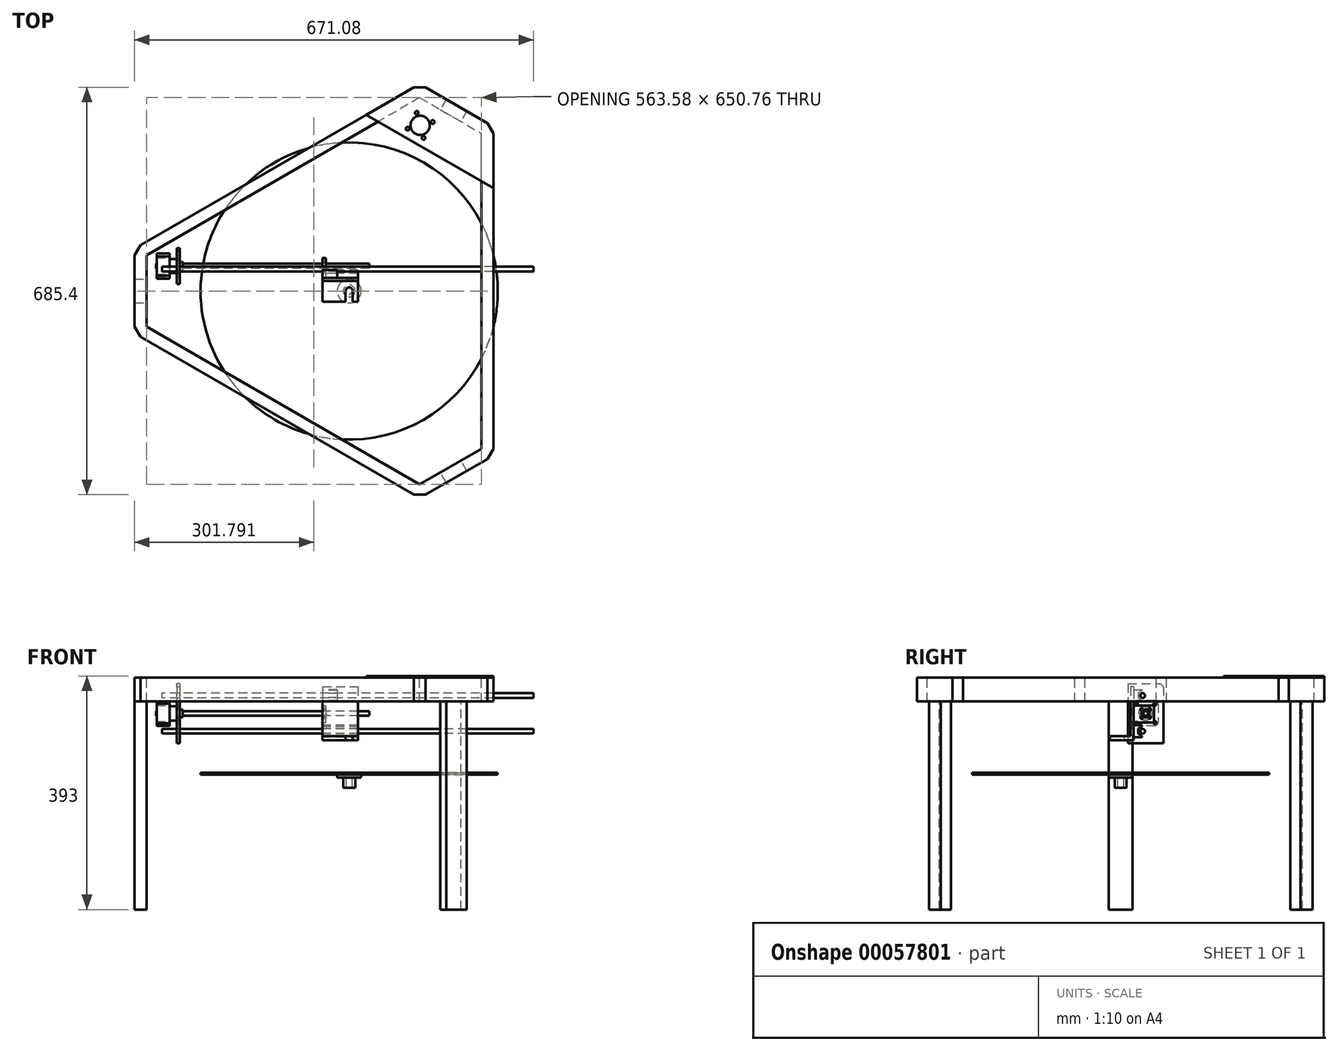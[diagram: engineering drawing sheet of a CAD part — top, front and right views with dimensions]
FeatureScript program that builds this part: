
annotation { "Feature Type Name" : "Feature", "Feature Type Description" : "" }
export const myFeature = defineFeature(function(context is Context, id is Id, definition is map)
    precondition{}
    {
        {
            var Q0;
            Q0=qCreatedBy(makeId("Right.planeOp"),FACE);
            var sketch = newSketch(context, id + "F0", { "sketchPlane" : qUnion([Q0])});
            skLineSegment(sketch, "E0.rect.bottom", {"start": v(21.15, 21.3) * mm, "end": v(-21.15, 21.3) * mm});
            skLineSegment(sketch, "E0.rect.top", {"start": v(21.15, -21.3) * mm, "end": v(-21.15, -21.3) * mm});
            skLineSegment(sketch, "E0.rect.left", {"start": v(21.15, 21.3) * mm, "end": v(21.15, -21.3) * mm});
            skLineSegment(sketch, "E0.rect.right", {"start": v(-21.15, 21.3) * mm, "end": v(-21.15, -21.3) * mm});
            skPoint(sketch, "E0.rect.middle", {"position": v(0, 0) * mm});
            skCircle(sketch, "E1", {"center": v(0, 0) * mm, "radius": 11 * mm});
            skCircle(sketch, "E2", {"center": v(0, 0) * mm, "radius": 4 * mm});
            skCircle(sketch, "E3", {"center": v(0, 0) * mm, "radius": 6.5 * mm});
            skCircle(sketch, "E4", {"center": v(0, 0) * mm, "radius": 12 * mm});
            skLineSegment(sketch, "E5", {"start": v(0, 0) * mm, "end": v(0, -54.1) * mm, "construction": true});
            skLineSegment(sketch, "E6", {"start": v(1.43, 0) * mm, "end": v(43.12, 0) * mm, "construction": true});
            skPoint(sketch, "E6.endSnap0", {"position": v(21.15, 0) * mm});
            skCircle(sketch, "E7", {"center": v(-15.5, -15.5) * mm, "radius": 2 * mm});
            skCircle(sketch, "E8.MirrorC", {"center": v(15.5, -15.5) * mm, "radius": 2 * mm});
            skCircle(sketch, "E9.MirrorC", {"center": v(-15.5, 15.5) * mm, "radius": 2 * mm});
            skCircle(sketch, "E10.MirrorC", {"center": v(15.5, 15.5) * mm, "radius": 2 * mm});
            skSolve(sketch);
        }
        {
            var Q0;
            Q0=makeQuery(id+"F0.imprint","IMPRINT",FACE,{"disambiguationData":[TD([[makeQuery(id+"F0.imprint","IMPRINT",EDGE,{"derivedFrom":sQuery(id+"F0.wireOp",EDGE,"E0.rect.bottom")}),1.0]])]});
            var Q1;
            Q1=makeQuery(id+"F0.imprint","IMPRINT",FACE,{"disambiguationData":[TD([[makeQuery(id+"F0.imprint","IMPRINT",EDGE,{"derivedFrom":sQuery(id+"F0.wireOp",EDGE,"E9.MirrorC")}),-1.0]])]});
            var Q2;
            Q2=makeQuery(id+"F0.imprint","IMPRINT",FACE,{"disambiguationData":[TD([[makeQuery(id+"F0.imprint","IMPRINT",EDGE,{"derivedFrom":sQuery(id+"F0.wireOp",EDGE,"E10.MirrorC")}),1.0]])]});
            var Q3;
            Q3=makeQuery(id+"F0.imprint","IMPRINT",FACE,{"disambiguationData":[TD([[makeQuery(id+"F0.imprint","IMPRINT",EDGE,{"derivedFrom":sQuery(id+"F0.wireOp",EDGE,"E8.MirrorC")}),-1.0]])]});
            var Q4;
            Q4=makeQuery(id+"F0.imprint","IMPRINT",FACE,{"disambiguationData":[TD([[makeQuery(id+"F0.imprint","IMPRINT",EDGE,{"derivedFrom":sQuery(id+"F0.wireOp",EDGE,"E7")}),1.0]])]});
            var Q5;
            Q5=makeQuery(id+"F0.imprint","IMPRINT",FACE,{"disambiguationData":[TD([[makeQuery(id+"F0.imprint","IMPRINT",EDGE,{"derivedFrom":sQuery(id+"F0.wireOp",EDGE,"E1")}),-1.0]])]});
            var Q6;
            Q6=makeQuery(id+"F0.imprint","IMPRINT",FACE,{"disambiguationData":[TD([[makeQuery(id+"F0.imprint","IMPRINT",EDGE,{"derivedFrom":sQuery(id+"F0.wireOp",EDGE,"E1")}),1.0]])]});
            var Q7;
            Q7=makeQuery(id+"F0.imprint","IMPRINT",FACE,{"disambiguationData":[TD([[makeQuery(id+"F0.imprint","IMPRINT",EDGE,{"derivedFrom":sQuery(id+"F0.wireOp",EDGE,"E2")}),-1.0]])]});
            extrude(context, id + "F1", {"entities" : qUnion([Q0, Q1, Q2, Q3, Q4, Q5, Q6, Q7]), "oppositeDirection" : true, "depth" : 34 * mm});
        }
        {
            var Q0;
            Q0=makeQuery(id+"F0.imprint","IMPRINT",FACE,{"disambiguationData":[TD([[makeQuery(id+"F0.imprint","IMPRINT",EDGE,{"derivedFrom":sQuery(id+"F0.wireOp",EDGE,"E2")}),1.0]])]});
            extrude(context, id + "F2", {"entities" : qUnion([Q0]), "depth" : 324 * mm, "hasSecondDirection" : true, "secondDirectionOppositeDirection" : true, "secondDirectionDepth" : 35 * mm});
        }
        {
            var Q0;
            Q0=makeQuery(id+"F0.imprint","IMPRINT",FACE,{"disambiguationData":[TD([[makeQuery(id+"F0.imprint","IMPRINT",EDGE,{"derivedFrom":sQuery(id+"F0.wireOp",EDGE,"E1")}),1.0]])]});
            var Q1;
            Q1=makeQuery(id+"F0.imprint","IMPRINT",FACE,{"disambiguationData":[TD([[makeQuery(id+"F0.imprint","IMPRINT",EDGE,{"derivedFrom":sQuery(id+"F0.wireOp",EDGE,"E2")}),-1.0]])]});
            extrude(context, id + "F3", {"entities" : qUnion([Q0, Q1]), "operationType" : NewBodyOperationType.ADD, "depth" : 2 * mm});
        }
        {
            var Q0;
            Q0=makeQuery(id+"F1.opExtrude","SWEPT_EDGE",EDGE,{"disambiguationData":[OSD([sQuery(id+"F0.wireOp",EDGE,"E0.rect.bottom"),sQuery(id+"F0.wireOp",EDGE,"E0.rect.left")])]});
            var Q1;
            Q1=makeQuery(id+"F1.opExtrude","SWEPT_EDGE",EDGE,{"disambiguationData":[OSD([sQuery(id+"F0.wireOp",EDGE,"E0.rect.top"),sQuery(id+"F0.wireOp",EDGE,"E0.rect.left")])]});
            var Q2;
            Q2=makeQuery(id+"F1.opExtrude","SWEPT_EDGE",EDGE,{"disambiguationData":[OSD([sQuery(id+"F0.wireOp",EDGE,"E0.rect.bottom"),sQuery(id+"F0.wireOp",EDGE,"E0.rect.right")])]});
            var Q3;
            Q3=makeQuery(id+"F1.opExtrude","SWEPT_EDGE",EDGE,{"disambiguationData":[OSD([sQuery(id+"F0.wireOp",EDGE,"E0.rect.top"),sQuery(id+"F0.wireOp",EDGE,"E0.rect.right")])]});
            chamfer(context, id + "F4", {"entities" : qUnion([Q0, Q1, Q2, Q3]), "width" : 5 * mm, "tangentPropagation" : true});
        }
        {
            var Q0;
            Q0=makeQuery(id+"F0.imprint","IMPRINT",FACE,{"disambiguationData":[TD([[makeQuery(id+"F0.imprint","IMPRINT",EDGE,{"derivedFrom":sQuery(id+"F0.wireOp",EDGE,"E10.MirrorC")}),1.0]])]});
            var Q1;
            Q1=makeQuery(id+"F0.imprint","IMPRINT",FACE,{"disambiguationData":[TD([[makeQuery(id+"F0.imprint","IMPRINT",EDGE,{"derivedFrom":sQuery(id+"F0.wireOp",EDGE,"E9.MirrorC")}),-1.0]])]});
            var Q2;
            Q2=makeQuery(id+"F0.imprint","IMPRINT",FACE,{"disambiguationData":[TD([[makeQuery(id+"F0.imprint","IMPRINT",EDGE,{"derivedFrom":sQuery(id+"F0.wireOp",EDGE,"E7")}),1.0]])]});
            var Q3;
            Q3=makeQuery(id+"F0.imprint","IMPRINT",FACE,{"disambiguationData":[TD([[makeQuery(id+"F0.imprint","IMPRINT",EDGE,{"derivedFrom":sQuery(id+"F0.wireOp",EDGE,"E8.MirrorC")}),-1.0]])]});
            extrude(context, id + "F5", {"entities" : qUnion([Q0, Q1, Q2, Q3]), "operationType" : NewBodyOperationType.REMOVE, "oppositeDirection" : true, "depth" : 12 * mm});
        }
        {
            var Q0;
            Q0=makeQuery(id+"F0.imprint","IMPRINT",FACE,{"disambiguationData":[TD([[makeQuery(id+"F0.imprint","IMPRINT",EDGE,{"derivedFrom":sQuery(id+"F0.wireOp",EDGE,"E2")}),-1.0]])]});
            extrude(context, id + "F6", {"entities" : qUnion([Q0]), "depth" : 10.2 * mm});
        }
        {
            var Q0;
            Q0=makeQuery(id+"F0.imprint","IMPRINT",FACE,{"disambiguationData":[TD([[makeQuery(id+"F0.imprint","IMPRINT",EDGE,{"derivedFrom":sQuery(id+"F0.wireOp",EDGE,"E1")}),1.0]])]});
            var Q1;
            Q1=makeQuery(id+"F0.imprint","IMPRINT",FACE,{"disambiguationData":[TD([[makeQuery(id+"F0.imprint","IMPRINT",EDGE,{"derivedFrom":sQuery(id+"F0.wireOp",EDGE,"E1")}),-1.0]])]});
            extrude(context, id + "F7", {"entities" : qUnion([Q0, Q1]), "operationType" : NewBodyOperationType.ADD, "depth" : 4.1 * mm});
        }
        {
            var Q0;
            Q0=qCreatedBy(makeId("Right.planeOp"),FACE);
            var sketch = newSketch(context, id + "F8", { "sketchPlane" : qUnion([Q0])});
            skCircle(sketch, "E11", {"center": v(0, 0) * mm, "radius": 9.5 * mm, "construction": true});
            skCircle(sketch, "E12", {"center": v(6.72, 6.72) * mm, "radius": 1.6 * mm});
            skLineSegment(sketch, "E13", {"start": v(0, 0) * mm, "end": v(21.23, 0) * mm, "construction": true});
            skLineSegment(sketch, "E14", {"start": v(0, 0) * mm, "end": v(0, 18.12) * mm, "construction": true});
            skLineSegment(sketch, "E15", {"start": v(0, 0) * mm, "end": v(6.72, 6.72) * mm, "construction": true});
            skCircle(sketch, "E16.MirrorC", {"center": v(6.72, -6.72) * mm, "radius": 1.6 * mm});
            skCircle(sketch, "E17.MirrorC", {"center": v(-6.72, 6.72) * mm, "radius": 1.6 * mm});
            skCircle(sketch, "E18.MirrorC", {"center": v(-6.72, -6.72) * mm, "radius": 1.6 * mm});
            skSolve(sketch);
        }
        {
            var Q0;
            Q0=qSketchRegion(id+"F8",true);
            extrude(context, id + "F9", {"entities" : qUnion([Q0]), "operationType" : NewBodyOperationType.REMOVE, "endBound" : BoundingType.THROUGH_ALL, "depth" : 25 * mm});
        }
        {
            var Q0;
            Q0=qCreatedBy(makeId("Top.planeOp"),FACE);
            var sketch = newSketch(context, id + "F10", { "sketchPlane" : qUnion([Q0])});
            skCircle(sketch, "E19", {"center": v(290, 0) * mm, "radius": 260 * mm, "construction": true});
            skLineSegment(sketch, "E20", {"start": v(0, 0) * mm, "end": v(0, 131.8) * mm, "construction": true});
            skLineSegment(sketch, "E21", {"start": v(290, 0) * mm, "end": v(290, -42) * mm, "construction": true});
            skCircle(sketch, "E22", {"center": v(290, -42) * mm, "radius": 250 * mm, "construction": true});
            skLineSegment(sketch, "E23.rect.bottom", {"start": v(305, -20) * mm, "end": v(245, -20) * mm});
            skLineSegment(sketch, "E23.rect.top", {"start": v(305, -60) * mm, "end": v(245, -60) * mm});
            skLineSegment(sketch, "E23.rect.left", {"start": v(305, -20) * mm, "end": v(305, -60) * mm});
            skLineSegment(sketch, "E23.rect.right", {"start": v(245, -20) * mm, "end": v(245, -60) * mm});
            skPoint(sketch, "E23.rect.middle", {"position": v(275, -40) * mm});
            skLineSegment(sketch, "E24", {"start": v(0, 0) * mm, "end": v(-84.34, 0) * mm, "construction": true});
            skLineSegment(sketch, "E25.bottom", {"start": v(245, -20) * mm, "end": v(269, -20) * mm});
            skLineSegment(sketch, "E25.top", {"start": v(245, 1.5) * mm, "end": v(269, 1.5) * mm});
            skLineSegment(sketch, "E25.left", {"start": v(245, -20) * mm, "end": v(245, 1.5) * mm});
            skLineSegment(sketch, "E25.right", {"start": v(269, -20) * mm, "end": v(269, 1.5) * mm});
            skLineSegment(sketch, "E26.bottom", {"start": v(305, -20) * mm, "end": v(281, -20) * mm});
            skLineSegment(sketch, "E26.top", {"start": v(305, 1.5) * mm, "end": v(281, 1.5) * mm});
            skLineSegment(sketch, "E26.left", {"start": v(305, -20) * mm, "end": v(305, 1.5) * mm});
            skLineSegment(sketch, "E26.right", {"start": v(281, -20) * mm, "end": v(281, 1.5) * mm});
            skLineSegment(sketch, "E27", {"start": v(245, -13.5) * mm, "end": v(269, -13.5) * mm});
            skLineSegment(sketch, "E28", {"start": v(281, -13.5) * mm, "end": v(290, -13.5) * mm});
            skPoint(sketch, "E28.startSnap0", {"position": v(257, -13.5) * mm});
            skLineSegment(sketch, "E29", {"start": v(257, -13.5) * mm, "end": v(257, 1.5) * mm});
            skPoint(sketch, "E30", {"position": v(257, -6) * mm});
            skLineSegment(sketch, "E31", {"start": v(491.95, -12) * mm, "end": v(676.1, -12) * mm, "construction": true});
            skLineSegment(sketch, "E32", {"start": v(257, -6) * mm, "end": v(462, -6) * mm, "construction": true});
            skLineSegment(sketch, "E33.rect.bottom", {"start": v(450, 1.5) * mm, "end": v(474, 1.5) * mm});
            skLineSegment(sketch, "E33.rect.top", {"start": v(450, -13.5) * mm, "end": v(474, -13.5) * mm});
            skLineSegment(sketch, "E33.rect.left", {"start": v(450, 1.5) * mm, "end": v(450, -13.5) * mm});
            skLineSegment(sketch, "E33.rect.right", {"start": v(474, 1.5) * mm, "end": v(474, -13.5) * mm});
            skPoint(sketch, "E33.rect.middle", {"position": v(462, -6) * mm});
            skLineSegment(sketch, "E34.rect.bottom", {"start": v(486, 1.5) * mm, "end": v(510, 1.5) * mm});
            skLineSegment(sketch, "E34.rect.top", {"start": v(486, -13.5) * mm, "end": v(510, -13.5) * mm});
            skLineSegment(sketch, "E34.rect.left", {"start": v(486, 1.5) * mm, "end": v(486, -13.5) * mm});
            skLineSegment(sketch, "E34.rect.right", {"start": v(510, 1.5) * mm, "end": v(510, -13.5) * mm});
            skPoint(sketch, "E34.rect.middle", {"position": v(498, -6) * mm});
            skPoint(sketch, "E34.rect.middle.positionSnap0", {"position": v(474, -6) * mm});
            skPoint(sketch, "E34.rect.centerSnap0", {"position": v(474, -6) * mm});
            skLineSegment(sketch, "E35.bottom", {"start": v(450, 8) * mm, "end": v(510, 8) * mm});
            skLineSegment(sketch, "E35.top", {"start": v(450, 48) * mm, "end": v(510, 48) * mm});
            skLineSegment(sketch, "E35.left", {"start": v(450, 8) * mm, "end": v(450, 48) * mm});
            skLineSegment(sketch, "E35.right", {"start": v(510, 8) * mm, "end": v(510, 48) * mm});
            skPoint(sketch, "E36", {"position": v(480, 48) * mm});
            skLineSegment(sketch, "E37", {"start": v(450, 8) * mm, "end": v(450, 1.5) * mm});
            skLineSegment(sketch, "E38", {"start": v(474, 1.5) * mm, "end": v(474, 8) * mm});
            skLineSegment(sketch, "E39", {"start": v(510, 1.5) * mm, "end": v(510, 8) * mm});
            skLineSegment(sketch, "E40", {"start": v(486, 1.5) * mm, "end": v(486, 8) * mm});
            skCircle(sketch, "E41", {"center": v(290, -42) * mm, "radius": 6 * mm});
            skCircle(sketch, "E42", {"center": v(465, 30) * mm, "radius": 10 * mm});
            skSolve(sketch);
        }
        {
            var Q0;
            Q0=qCreatedBy(makeId("Right.planeOp"),FACE);
            var sketch = newSketch(context, id + "F11", { "sketchPlane" : qUnion([Q0])});
            skCircle(sketch, "E43", {"center": v(-5, 30) * mm, "radius": 4 * mm});
            skCircle(sketch, "E44", {"center": v(-5, -30) * mm, "radius": 4 * mm});
            skLineSegment(sketch, "E45", {"start": v(0, 0) * mm, "end": v(-59.05, 0) * mm, "construction": true});
            skLineSegment(sketch, "E46.bottom", {"start": v(-11, 37) * mm, "end": v(-13, 37) * mm, "construction": true});
            skLineSegment(sketch, "E46.top", {"start": v(-11, -45) * mm, "end": v(-13, -45) * mm, "construction": true});
            skLineSegment(sketch, "E46.left", {"start": v(-11, 37) * mm, "end": v(-11, -45) * mm, "construction": true});
            skLineSegment(sketch, "E46.right", {"start": v(-13, 37) * mm, "end": v(-13, -45) * mm, "construction": true});
            skLineSegment(sketch, "E47", {"start": v(-5, 4.78) * mm, "end": v(-5, 49.26) * mm, "construction": true});
            skLineSegment(sketch, "E48", {"start": v(0, 0) * mm, "end": v(0, 64.82) * mm, "construction": true});
            skLineSegment(sketch, "E49.bottom", {"start": v(-11, -45) * mm, "end": v(-51, -45) * mm, "construction": true});
            skLineSegment(sketch, "E49.top", {"start": v(-11, -43) * mm, "end": v(-51, -43) * mm, "construction": true});
            skLineSegment(sketch, "E49.left", {"start": v(-11, -45) * mm, "end": v(-11, -43) * mm, "construction": true});
            skLineSegment(sketch, "E49.right", {"start": v(-51, -45) * mm, "end": v(-51, -43) * mm, "construction": true});
            skSolve(sketch);
        }
        {
            var Q0;
            Q0=qSketchRegion(id+"F11",true);
            extrude(context, id + "F12", {"entities" : qUnion([Q0]), "depth" : 600 * mm, "hasSecondDirection" : true, "secondDirectionOppositeDirection" : true, "secondDirectionDepth" : 25 * mm});
        }
        {
            var Q0;
            Q0=qCreatedBy(makeId("Top.planeOp"),FACE);
            cPlane(context, id + "F13", {"entities" : qUnion([Q0]), "cplaneType" : CPlaneType.OFFSET, "offset" : 45 * mm, "oppositeDirection" : true, "width" : 150 * mm, "height" : 150 * mm});
        }
        {
            var Q0;
            Q0=qCreatedBy(id+"F13.planeOp",FACE);
            var sketch = newSketch(context, id + "F14", { "sketchPlane" : qUnion([Q0])});
            skLineSegment(sketch, "E50.bottom", {"start": v(245, -20) * mm, "end": v(305, -20) * mm});
            skLineSegment(sketch, "E50.top", {"start": v(245, -60) * mm, "end": v(305, -60) * mm});
            skLineSegment(sketch, "E50.left", {"start": v(245, -20) * mm, "end": v(245, -60) * mm});
            skLineSegment(sketch, "E50.right", {"start": v(305, -20) * mm, "end": v(305, -60) * mm});
            skCircle(sketch, "E51", {"center": v(290, -42) * mm, "radius": 6 * mm});
            skLineSegment(sketch, "E52", {"start": v(284, -42) * mm, "end": v(284, -60) * mm});
            skLineSegment(sketch, "E53", {"start": v(296, -42) * mm, "end": v(296, -60) * mm});
            skSolve(sketch);
        }
        {
            var Q0;
            Q0=makeQuery(id+"F14.imprint","IMPRINT",FACE,{"disambiguationData":[TD([[makeQuery(id+"F14.imprint","IMPRINT",EDGE,{"derivedFrom":sQuery(id+"F14.wireOp",EDGE,"E50.bottom")}),-1.0]])]});
            extrude(context, id + "F15", {"entities" : qUnion([Q0]), "depth" : 90 * mm});
        }
        {
            var Q0;
            Q0=makeQuery(id+"F15.opExtrude","SWEPT_FACE",FACE,{"disambiguationData":[OSD([sQuery(id+"F14.wireOp",EDGE,"E50.right")])]});
            var sketch = newSketch(context, id + "F16", { "sketchPlane" : qUnion([Q0])});
            skLineSegment(sketch, "E54.bottom", {"start": v(-60, 45) * mm, "end": v(-25, 45) * mm});
            skLineSegment(sketch, "E54.top", {"start": v(-60, -38) * mm, "end": v(-25, -38) * mm});
            skLineSegment(sketch, "E54.left", {"start": v(-60, 45) * mm, "end": v(-60, -38) * mm});
            skLineSegment(sketch, "E54.right", {"start": v(-25, 45) * mm, "end": v(-25, -38) * mm});
            skSolve(sketch);
        }
        {
            var Q0;
            Q0=qSketchRegion(id+"F16",true);
            extrude(context, id + "F17", {"entities" : qUnion([Q0]), "operationType" : NewBodyOperationType.REMOVE, "endBound" : BoundingType.THROUGH_ALL, "oppositeDirection" : true, "depth" : 25 * mm});
        }
        {
            var Q0;
            Q0=makeQuery(id+"F15.opExtrude","SWEPT_FACE",FACE,{"disambiguationData":[OSD([sQuery(id+"F14.wireOp",EDGE,"E50.left")])]});
            var sketch = newSketch(context, id + "F18", { "sketchPlane" : qUnion([Q0])});
            skLineSegment(sketch, "E55.bottom", {"start": v(25, 13.6) * mm, "end": v(-13.78, 13.6) * mm});
            skLineSegment(sketch, "E55.top", {"start": v(25, -15.13) * mm, "end": v(-13.78, -15.13) * mm});
            skLineSegment(sketch, "E55.left", {"start": v(25, 13.6) * mm, "end": v(25, -15.13) * mm});
            skLineSegment(sketch, "E55.right", {"start": v(-13.78, 13.6) * mm, "end": v(-13.78, -15.13) * mm});
            skCircle(sketch, "E56", {"center": v(0, 0) * mm, "radius": 6.75 * mm});
            skCircle(sketch, "E57", {"center": v(-6.72, 6.72) * mm, "radius": 2.25 * mm});
            skCircle(sketch, "E58", {"center": v(6.72, 6.72) * mm, "radius": 2.25 * mm});
            skCircle(sketch, "E59", {"center": v(6.72, -6.72) * mm, "radius": 2.25 * mm});
            skCircle(sketch, "E60", {"center": v(-6.72, -6.72) * mm, "radius": 2.25 * mm});
            skSolve(sketch);
        }
        {
            var Q0;
            Q0=qSketchRegion(id+"F18",true);
            var Q1;
            Q1=makeQuery(id+"F1.opExtrude","CAP_FACE",FACE,{"disambiguationData":[OSD([sQuery(id+"F0.wireOp",EDGE,"E0.rect.bottom"),sQuery(id+"F0.wireOp",EDGE,"E0.rect.top"),sQuery(id+"F0.wireOp",EDGE,"E0.rect.left"),sQuery(id+"F0.wireOp",EDGE,"E0.rect.right"),sQuery(id+"F0.wireOp",EDGE,"E2")])],"isStart":false});
            extrude(context, id + "F19", {"entities" : qUnion([Q0, Q1]), "operationType" : NewBodyOperationType.ADD, "oppositeDirection" : true, "depth" : 6 * mm});
        }
        {
            var Q0;
            Q0=makeQuery(id+"F19.boolean.opBoolean","MERGE",FACE,{"derivedFrom":[makeQuery(id+"F15.opExtrude","SWEPT_FACE",FACE,{"disambiguationData":[OSD([sQuery(id+"F14.wireOp",EDGE,"E50.left")])]}),makeQuery(id+"F19.opExtrude","CAP_FACE",FACE,{"disambiguationData":[OSD([sQuery(id+"F18.wireOp",EDGE,"E55.bottom"),sQuery(id+"F18.wireOp",EDGE,"E55.top"),sQuery(id+"F18.wireOp",EDGE,"E55.left"),sQuery(id+"F18.wireOp",EDGE,"E55.right"),sQuery(id+"F18.wireOp",EDGE,"E56"),sQuery(id+"F18.wireOp",EDGE,"E57"),sQuery(id+"F18.wireOp",EDGE,"E58"),sQuery(id+"F18.wireOp",EDGE,"E59"),sQuery(id+"F18.wireOp",EDGE,"E60")])],"isStart":true})]});
            var sketch = newSketch(context, id + "F20", { "sketchPlane" : qUnion([Q0])});
            skCircle(sketch, "E61", {"center": v(5, -30) * mm, "radius": 7.5 * mm, "construction": true});
            skCircle(sketch, "E62", {"center": v(5, 30) * mm, "radius": 7.5 * mm, "construction": true});
            skLineSegment(sketch, "E63", {"start": v(6.5, -22.2) * mm, "end": v(12.6, -25.73) * mm});
            skLineSegment(sketch, "E64", {"start": v(12.6, -25.73) * mm, "end": v(12.6, -34.27) * mm});
            skLineSegment(sketch, "E65", {"start": v(12.6, -34.27) * mm, "end": v(6.5, -37.8) * mm});
            skLineSegment(sketch, "E66", {"start": v(6.5, -37.8) * mm, "end": v(6.5, -40) * mm});
            skLineSegment(sketch, "E67", {"start": v(6.5, -40) * mm, "end": v(20, -40) * mm});
            skLineSegment(sketch, "E68", {"start": v(20, -40) * mm, "end": v(20, -20) * mm});
            skLineSegment(sketch, "E69", {"start": v(20, -20) * mm, "end": v(6.5, -20) * mm});
            skLineSegment(sketch, "E70", {"start": v(6.5, -20) * mm, "end": v(6.5, -22.2) * mm});
            skLineSegment(sketch, "E71", {"start": v(5, -30) * mm, "end": v(15.81, -30) * mm, "construction": true});
            skLineSegment(sketch, "E72", {"start": v(5, -30) * mm, "end": v(5, -33.48) * mm, "construction": true});
            skPoint(sketch, "E73", {"position": v(12.6, -30) * mm});
            skPoint(sketch, "E74", {"position": v(12.5, -30) * mm});
            skPoint(sketch, "E75", {"position": v(20, -30) * mm});
            skPoint(sketch, "E76", {"position": v(13.46, -30) * mm});
            skSolve(sketch);
        }
        {
            var Q0;
            Q0=qSketchRegion(id+"F20",true);
            extrude(context, id + "F21", {"entities" : qUnion([Q0]), "oppositeDirection" : true, "depth" : 60 * mm});
        }
        {
            var Q0;
            Q0=qCreatedBy(makeId("Right.planeOp"),FACE);
            var sketch = newSketch(context, id + "F22", { "sketchPlane" : qUnion([Q0])});
            skLineSegment(sketch, "E77.bottom", {"start": v(-30, 50) * mm, "end": v(30, 50) * mm});
            skLineSegment(sketch, "E77.top", {"start": v(-30, -50) * mm, "end": v(30, -50) * mm});
            skLineSegment(sketch, "E77.left", {"start": v(-30, 50) * mm, "end": v(-30, -50) * mm});
            skLineSegment(sketch, "E77.right", {"start": v(30, 50) * mm, "end": v(30, -50) * mm});
            skCircle(sketch, "E78", {"center": v(-5, 30) * mm, "radius": 4 * mm});
            skCircle(sketch, "E79", {"center": v(-5, -30) * mm, "radius": 4 * mm});
            skCircle(sketch, "E80", {"center": v(-15.5, -15.5) * mm, "radius": 2.5 * mm});
            skCircle(sketch, "E81", {"center": v(-15.5, 15.5) * mm, "radius": 2.5 * mm});
            skCircle(sketch, "E82", {"center": v(15.5, 15.5) * mm, "radius": 2.5 * mm});
            skLineSegment(sketch, "E83", {"start": v(0, 0) * mm, "end": v(0, -53.03) * mm, "construction": true});
            skLineSegment(sketch, "E84", {"start": v(0, 0) * mm, "end": v(44.98, 0) * mm, "construction": true});
            skCircle(sketch, "E85", {"center": v(15.5, -15.5) * mm, "radius": 2.5 * mm});
            skCircle(sketch, "E86", {"center": v(0, 0) * mm, "radius": 11 * mm});
            skSolve(sketch);
        }
        {
            var Q0;
            Q0=qSketchRegion(id+"F22",true);
            extrude(context, id + "F23", {"entities" : qUnion([Q0]), "depth" : 5 * mm});
        }
        {
            var Q0;
            Q0=makeQuery(id+"F23.opExtrude","SWEPT_EDGE",EDGE,{"disambiguationData":[OSD([sQuery(id+"F22.wireOp",EDGE,"E77.bottom"),sQuery(id+"F22.wireOp",EDGE,"E77.right")])]});
            chamfer(context, id + "F24", {"entities" : qUnion([Q0]), "width" : 5 * mm, "tangentPropagation" : true});
        }
        {
            var Q0;
            Q0=makeQuery(id+"F20.imprint","IMPRINT",FACE,{"disambiguationData":[TD([[makeQuery(id+"F20.imprint","IMPRINT",EDGE,{"derivedFrom":sQuery(id+"F20.wireOp",EDGE,"E63")}),1.0]])]});
            var sketch = newSketch(context, id + "F25", { "sketchPlane" : qUnion([Q0])});
            skLineSegment(sketch, "E87.bottom", {"start": v(20, 40) * mm, "end": v(6.5, 40) * mm});
            skLineSegment(sketch, "E87.top", {"start": v(20, 20) * mm, "end": v(6.5, 20) * mm});
            skLineSegment(sketch, "E87.left", {"start": v(20, 40) * mm, "end": v(20, 20) * mm});
            skLineSegment(sketch, "E87.right", {"start": v(6.5, 40) * mm, "end": v(6.5, 20) * mm});
            skPoint(sketch, "E88", {"position": v(20, 30) * mm});
            skLineSegment(sketch, "E89", {"start": v(6.5, 38.53) * mm, "end": v(12.6, 33.41) * mm});
            skLineSegment(sketch, "E90", {"start": v(12.6, 33.41) * mm, "end": v(12.6, 26.59) * mm});
            skLineSegment(sketch, "E91", {"start": v(12.6, 26.59) * mm, "end": v(6.5, 21.47) * mm});
            skPoint(sketch, "E92", {"position": v(12.6, 30) * mm});
            skSolve(sketch);
        }
        {
            var Q0;
            {var subQ1=sQuery(id+"F25.wireOp",EDGE,"E87.bottom");Q0=makeQuery(id+"F25.imprint","IMPRINT",FACE,{"disambiguationData":[TD([[makeQuery(id+"F25.imprint","IMPRINT",EDGE,{"derivedFrom":subQ1}),1.0]])]});}
            extrude(context, id + "F26", {"entities" : qUnion([Q0]), "oppositeDirection" : true, "depth" : 25 * mm});
        }
        {
            var Q0;
            Q0=qCreatedBy(makeId("Top.planeOp"),FACE);
            cPlane(context, id + "F27", {"entities" : qUnion([Q0]), "cplaneType" : CPlaneType.OFFSET, "offset" : 100 * mm, "oppositeDirection" : true, "width" : 150 * mm, "height" : 150 * mm});
        }
        {
            var Q0;
            Q0=qCreatedBy(id+"F27.planeOp",FACE);
            var sketch = newSketch(context, id + "F28", { "sketchPlane" : qUnion([Q0])});
            skCircle(sketch, "E93", {"center": v(290, -42) * mm, "radius": 250 * mm});
            skCircle(sketch, "E94", {"center": v(290, -42) * mm, "radius": 20 * mm});
            skCircle(sketch, "E95", {"center": v(290, -42) * mm, "radius": 10 * mm});
            skCircle(sketch, "E96", {"center": v(290, -42) * mm, "radius": 5 * mm});
            skSolve(sketch);
        }
        {
            var Q0;
            Q0=qSketchRegion(id+"F28",true);
            var Q1;
            Q1=makeQuery(id+"F28.imprint","IMPRINT",FACE,{"disambiguationData":[TD([[makeQuery(id+"F28.imprint","IMPRINT",EDGE,{"derivedFrom":sQuery(id+"F28.wireOp",EDGE,"E94")}),1.0]])]});
            var Q2;
            Q2=makeQuery(id+"F28.imprint","IMPRINT",FACE,{"disambiguationData":[TD([[makeQuery(id+"F28.imprint","IMPRINT",EDGE,{"derivedFrom":sQuery(id+"F28.wireOp",EDGE,"E95")}),1.0]])]});
            var Q3;
            Q3=makeQuery(id+"F28.imprint","IMPRINT",FACE,{"disambiguationData":[TD([[makeQuery(id+"F28.imprint","IMPRINT",EDGE,{"derivedFrom":sQuery(id+"F28.wireOp",EDGE,"E96")}),1.0]])]});
            extrude(context, id + "F29", {"entities" : qUnion([Q0, Q1, Q2, Q3]), "oppositeDirection" : true, "depth" : 3 * mm});
        }
        {
            var Q0;
            Q0=makeQuery(id+"F28.imprint","IMPRINT",FACE,{"disambiguationData":[TD([[makeQuery(id+"F28.imprint","IMPRINT",EDGE,{"derivedFrom":sQuery(id+"F28.wireOp",EDGE,"E94")}),1.0]])]});
            var Q1;
            Q1=makeQuery(id+"F28.imprint","IMPRINT",FACE,{"disambiguationData":[TD([[makeQuery(id+"F28.imprint","IMPRINT",EDGE,{"derivedFrom":sQuery(id+"F28.wireOp",EDGE,"E95")}),1.0]])]});
            extrude(context, id + "F30", {"entities" : qUnion([Q0, Q1]), "oppositeDirection" : true, "depth" : 8 * mm, "hasSecondDirection" : true, "secondDirectionOppositeDirection" : true, "secondDirectionDepth" : 3 * mm});
        }
        {
            var Q0;
            Q0=makeQuery(id+"F28.imprint","IMPRINT",FACE,{"disambiguationData":[TD([[makeQuery(id+"F28.imprint","IMPRINT",EDGE,{"derivedFrom":sQuery(id+"F28.wireOp",EDGE,"E95")}),1.0]])]});
            extrude(context, id + "F31", {"entities" : qUnion([Q0]), "operationType" : NewBodyOperationType.ADD, "oppositeDirection" : true, "depth" : 25 * mm, "hasSecondDirection" : true, "secondDirectionOppositeDirection" : true, "secondDirectionDepth" : 3 * mm});
        }
        {
            var Q0;
            Q0=qCreatedBy(makeId("Top.planeOp"),FACE);
            cPlane(context, id + "F32", {"entities" : qUnion([Q0]), "cplaneType" : CPlaneType.OFFSET, "offset" : 60 * mm, "width" : 150 * mm, "height" : 150 * mm});
        }
        {
            var Q0;
            Q0=qCreatedBy(id+"F32.planeOp",FACE);
            var sketch = newSketch(context, id + "F33", { "sketchPlane" : qUnion([Q0])});
            skCircle(sketch, "E97", {"center": v(290, -42) * mm, "radius": 232.5 * mm, "construction": true});
            skLineSegment(sketch, "E98", {"start": v(522.5, 360.7) * mm, "end": v(-175, -42) * mm, "construction": true});
            skLineSegment(sketch, "E99", {"start": v(-175, -42) * mm, "end": v(522.5, -444.7) * mm, "construction": true});
            skLineSegment(sketch, "E100", {"start": v(522.5, -444.7) * mm, "end": v(522.5, 360.7) * mm, "construction": true});
            skLineSegment(sketch, "E101", {"start": v(290, -42) * mm, "end": v(-175, -42) * mm, "construction": true});
            skLineSegment(sketch, "E102", {"start": v(290, -42) * mm, "end": v(290, -153.21) * mm, "construction": true});
            skLineSegment(sketch, "E103.0", {"start": v(398.58, 300.7) * mm, "end": v(-61.08, 35.32) * mm});
            skLineSegment(sketch, "E103.1", {"start": v(532.5, -307.38) * mm, "end": v(532.5, 223.38) * mm});
            skLineSegment(sketch, "E103.2", {"start": v(-61.08, -119.32) * mm, "end": v(398.58, -384.7) * mm});
            skLineSegment(sketch, "E104.0", {"start": v(408.58, 283.38) * mm, "end": v(-51.08, 18) * mm});
            skLineSegment(sketch, "E104.1", {"start": v(512.5, -307.38) * mm, "end": v(512.5, 223.38) * mm});
            skLineSegment(sketch, "E104.2", {"start": v(-51.08, -102) * mm, "end": v(408.58, -367.38) * mm});
            skLineSegment(sketch, "E105", {"start": v(408.58, 283.38) * mm, "end": v(512.5, 223.38) * mm});
            skLineSegment(sketch, "E106", {"start": v(460.54, 253.38) * mm, "end": v(290, -42) * mm, "construction": true});
            skPoint(sketch, "E107", {"position": v(408.58, 283.38) * mm});
            skPoint(sketch, "E108", {"position": v(512.5, 223.38) * mm});
            skLineSegment(sketch, "E109", {"start": v(408.58, 283.38) * mm, "end": v(398.58, 300.7) * mm});
            skLineSegment(sketch, "E110", {"start": v(512.5, 223.38) * mm, "end": v(532.5, 223.38) * mm});
            skLineSegment(sketch, "E111", {"start": v(408.58, 283.38) * mm, "end": v(418.58, 300.7) * mm});
            skLineSegment(sketch, "E112", {"start": v(418.58, 300.7) * mm, "end": v(522.5, 240.7) * mm});
            skLineSegment(sketch, "E113", {"start": v(522.5, 240.7) * mm, "end": v(512.5, 223.38) * mm});
            skCircle(sketch, "E114", {"center": v(290, -42) * mm, "radius": 341.08 * mm, "construction": true});
            skLineSegment(sketch, "E115", {"start": v(408.58, -367.38) * mm, "end": v(512.5, -307.38) * mm});
            skLineSegment(sketch, "E116", {"start": v(290, -42) * mm, "end": v(460.54, -337.38) * mm, "construction": true});
            skLineSegment(sketch, "E117", {"start": v(408.58, -367.38) * mm, "end": v(418.58, -384.7) * mm});
            skLineSegment(sketch, "E118", {"start": v(418.58, -384.7) * mm, "end": v(522.5, -324.7) * mm});
            skLineSegment(sketch, "E119", {"start": v(522.5, -324.7) * mm, "end": v(512.5, -307.38) * mm});
            skLineSegment(sketch, "E120", {"start": v(512.5, -307.38) * mm, "end": v(532.5, -307.38) * mm});
            skLineSegment(sketch, "E121", {"start": v(408.58, -367.38) * mm, "end": v(398.58, -384.7) * mm});
            skLineSegment(sketch, "E122", {"start": v(-51.08, 18) * mm, "end": v(-51.08, -102) * mm});
            skPoint(sketch, "E123", {"position": v(-51.08, -42) * mm});
            skLineSegment(sketch, "E124", {"start": v(-71.08, 18) * mm, "end": v(-71.08, -102) * mm});
            skLineSegment(sketch, "E125", {"start": v(-51.08, -102) * mm, "end": v(-61.08, -119.32) * mm});
            skLineSegment(sketch, "E126", {"start": v(-51.08, 18) * mm, "end": v(-61.08, 35.32) * mm});
            skLineSegment(sketch, "E127", {"start": v(398.58, -384.7) * mm, "end": v(418.58, -384.7) * mm});
            skLineSegment(sketch, "E128", {"start": v(532.5, -307.38) * mm, "end": v(522.5, -324.7) * mm});
            skLineSegment(sketch, "E129", {"start": v(398.58, 300.7) * mm, "end": v(418.58, 300.7) * mm});
            skLineSegment(sketch, "E130", {"start": v(522.5, 240.7) * mm, "end": v(532.5, 223.38) * mm});
            skPoint(sketch, "E131.orphan", {"position": v(522.5, 217.6) * mm});
            skPoint(sketch, "E132.orphan", {"position": v(398.58, 289.15) * mm});
            skLineSegment(sketch, "E133", {"start": v(-71.08, 18) * mm, "end": v(-51.08, 18) * mm});
            skLineSegment(sketch, "E134", {"start": v(-71.08, -102) * mm, "end": v(-51.08, -102) * mm});
            skLineSegment(sketch, "E135", {"start": v(-71.08, 18) * mm, "end": v(-61.08, 35.32) * mm});
            skLineSegment(sketch, "E136", {"start": v(-71.08, -102) * mm, "end": v(-61.08, -119.32) * mm});
            skSolve(sketch);
        }
        {
            var Q0;
            Q0=makeQuery(id+"F33.imprint","IMPRINT",FACE,{"disambiguationData":[TD([[makeQuery(id+"F33.imprint","IMPRINT",EDGE,{"derivedFrom":sQuery(id+"F33.wireOp",EDGE,"E105")}),1.0]])]});
            var Q1;
            Q1=makeQuery(id+"F33.imprint","IMPRINT",FACE,{"disambiguationData":[TD([[makeQuery(id+"F33.imprint","IMPRINT",EDGE,{"derivedFrom":sQuery(id+"F33.wireOp",EDGE,"E110")}),1.0]])]});
            var Q2;
            Q2=makeQuery(id+"F33.imprint","IMPRINT",FACE,{"disambiguationData":[TD([[makeQuery(id+"F33.imprint","IMPRINT",EDGE,{"derivedFrom":sQuery(id+"F33.wireOp",EDGE,"E103.1")}),1.0]])]});
            var Q3;
            Q3=makeQuery(id+"F33.imprint","IMPRINT",FACE,{"disambiguationData":[TD([[makeQuery(id+"F33.imprint","IMPRINT",EDGE,{"derivedFrom":sQuery(id+"F33.wireOp",EDGE,"E119")}),-1.0]])]});
            var Q4;
            Q4=makeQuery(id+"F33.imprint","IMPRINT",FACE,{"disambiguationData":[TD([[makeQuery(id+"F33.imprint","IMPRINT",EDGE,{"derivedFrom":sQuery(id+"F33.wireOp",EDGE,"E115")}),-1.0]])]});
            var Q5;
            Q5=makeQuery(id+"F33.imprint","IMPRINT",FACE,{"disambiguationData":[TD([[makeQuery(id+"F33.imprint","IMPRINT",EDGE,{"derivedFrom":sQuery(id+"F33.wireOp",EDGE,"E117")}),-1.0]])]});
            var Q6;
            Q6=makeQuery(id+"F33.imprint","IMPRINT",FACE,{"disambiguationData":[TD([[makeQuery(id+"F33.imprint","IMPRINT",EDGE,{"derivedFrom":sQuery(id+"F33.wireOp",EDGE,"E103.2")}),1.0]])]});
            var Q7;
            {var subQ2=sQuery(id+"F33.wireOp",EDGE,"E125");Q7=makeQuery(id+"F33.imprint","IMPRINT",FACE,{"disambiguationData":[TD([[makeQuery(id+"F33.imprint","IMPRINT",EDGE,{"derivedFrom":subQ2}),-1.0]])]});}
            var Q8;
            {var subQ2=sQuery(id+"F33.wireOp",EDGE,"E122");Q8=makeQuery(id+"F33.imprint","IMPRINT",FACE,{"disambiguationData":[TD([[makeQuery(id+"F33.imprint","IMPRINT",EDGE,{"derivedFrom":subQ2}),-1.0]])]});}
            var Q9;
            {var subQ2=sQuery(id+"F33.wireOp",EDGE,"E126");Q9=makeQuery(id+"F33.imprint","IMPRINT",FACE,{"disambiguationData":[TD([[makeQuery(id+"F33.imprint","IMPRINT",EDGE,{"derivedFrom":subQ2}),1.0]])]});}
            var Q10;
            Q10=makeQuery(id+"F33.imprint","IMPRINT",FACE,{"disambiguationData":[TD([[makeQuery(id+"F33.imprint","IMPRINT",EDGE,{"derivedFrom":sQuery(id+"F33.wireOp",EDGE,"E103.0")}),1.0]])]});
            var Q11;
            Q11=makeQuery(id+"F33.imprint","IMPRINT",FACE,{"disambiguationData":[TD([[makeQuery(id+"F33.imprint","IMPRINT",EDGE,{"derivedFrom":sQuery(id+"F33.wireOp",EDGE,"E109")}),-1.0]])]});
            extrude(context, id + "F34", {"entities" : qUnion([Q0, Q1, Q2, Q3, Q4, Q5, Q6, Q7, Q8, Q9, Q10, Q11]), "oppositeDirection" : true, "depth" : 40 * mm});
        }
        {
            var Q0;
            Q0=makeQuery(id+"F34.opExtrude","CAP_FACE",FACE,{"disambiguationData":[OSD([sQuery(id+"F33.wireOp",EDGE,"E103.0"),sQuery(id+"F33.wireOp",EDGE,"E103.1"),sQuery(id+"F33.wireOp",EDGE,"E103.2"),sQuery(id+"F33.wireOp",EDGE,"E104.0"),sQuery(id+"F33.wireOp",EDGE,"E104.1"),sQuery(id+"F33.wireOp",EDGE,"E104.2"),sQuery(id+"F33.wireOp",EDGE,"E105"),sQuery(id+"F33.wireOp",EDGE,"E112"),sQuery(id+"F33.wireOp",EDGE,"E115"),sQuery(id+"F33.wireOp",EDGE,"E118"),sQuery(id+"F33.wireOp",EDGE,"E122"),sQuery(id+"F33.wireOp",EDGE,"E124"),sQuery(id+"F33.wireOp",EDGE,"E127"),sQuery(id+"F33.wireOp",EDGE,"E128"),sQuery(id+"F33.wireOp",EDGE,"E129"),sQuery(id+"F33.wireOp",EDGE,"E130"),sQuery(id+"F33.wireOp",EDGE,"0wcdNtPX-tNnW-twyc-Lb4C-ySeZqgfmw5Zl"),sQuery(id+"F33.wireOp",EDGE,"qDnOeYNK-LT1R-1873-xmuX-v1TuTv1v70i1")])],"isStart":false});
            var sketch = newSketch(context, id + "F35", { "sketchPlane" : qUnion([Q0])});
            skLineSegment(sketch, "E137.bottom", {"start": v(-71.08, 62) * mm, "end": v(-51.08, 62) * mm});
            skLineSegment(sketch, "E137.top", {"start": v(-71.08, 22) * mm, "end": v(-51.08, 22) * mm});
            skLineSegment(sketch, "E137.left", {"start": v(-71.08, 62) * mm, "end": v(-71.08, 22) * mm});
            skLineSegment(sketch, "E137.right", {"start": v(-51.08, 62) * mm, "end": v(-51.08, 22) * mm});
            skPoint(sketch, "E138", {"position": v(-51.08, 42) * mm});
            skLineSegment(sketch, "E139.bottom", {"start": v(453.22, -280.7) * mm, "end": v(487.86, -260.7) * mm});
            skLineSegment(sketch, "E139.top", {"start": v(443.22, -263.38) * mm, "end": v(477.86, -243.38) * mm});
            skLineSegment(sketch, "E139.left", {"start": v(453.22, -280.7) * mm, "end": v(443.22, -263.38) * mm});
            skLineSegment(sketch, "E139.right", {"start": v(487.86, -260.7) * mm, "end": v(477.86, -243.38) * mm});
            skPoint(sketch, "E140", {"position": v(460.54, -253.38) * mm});
            skLineSegment(sketch, "E141.bottom", {"start": v(453.22, 364.7) * mm, "end": v(487.86, 344.7) * mm});
            skLineSegment(sketch, "E141.top", {"start": v(443.22, 347.38) * mm, "end": v(477.86, 327.38) * mm});
            skLineSegment(sketch, "E141.left", {"start": v(453.22, 364.7) * mm, "end": v(443.22, 347.38) * mm});
            skLineSegment(sketch, "E141.right", {"start": v(487.86, 344.7) * mm, "end": v(477.86, 327.38) * mm});
            skPoint(sketch, "E142", {"position": v(460.54, 337.38) * mm});
            skSolve(sketch);
        }
        {
            var Q0;
            Q0=qSketchRegion(id+"F35",true);
            extrude(context, id + "F36", {"entities" : qUnion([Q0]), "depth" : 350 * mm});
        }
        {
            var Q0;
            Q0=makeQuery(id+"F33.imprint","IMPRINT",FACE,{"disambiguationData":[TD([[makeQuery(id+"F33.imprint","IMPRINT",EDGE,{"derivedFrom":sQuery(id+"F33.wireOp",EDGE,"E105")}),1.0]])]});
            var sketch = newSketch(context, id + "F37", { "sketchPlane" : qUnion([Q0])});
            skLineSegment(sketch, "E143", {"start": v(532.5, 131) * mm, "end": v(532.5, 223.38) * mm});
            skLineSegment(sketch, "E144", {"start": v(532.5, 223.38) * mm, "end": v(522.5, 240.7) * mm});
            skLineSegment(sketch, "E145", {"start": v(522.5, 240.7) * mm, "end": v(418.58, 300.7) * mm});
            skLineSegment(sketch, "E146", {"start": v(418.58, 300.7) * mm, "end": v(398.58, 300.7) * mm});
            skLineSegment(sketch, "E147", {"start": v(398.58, 300.7) * mm, "end": v(318.58, 254.51) * mm});
            skLineSegment(sketch, "E148", {"start": v(318.58, 254.51) * mm, "end": v(532.5, 131) * mm});
            skCircle(sketch, "E149", {"center": v(409.36, 236.74) * mm, "radius": 16.22 * mm});
            skCircle(sketch, "E150", {"center": v(388.27, 231.09) * mm, "radius": 3 * mm});
            skLineSegment(sketch, "E151", {"start": v(409.36, 236.74) * mm, "end": v(387.87, 199.51) * mm, "construction": true});
            skLineSegment(sketch, "E152", {"start": v(409.36, 236.74) * mm, "end": v(437.81, 220.31) * mm, "construction": true});
            skLineSegment(sketch, "E153", {"start": v(388.27, 231.09) * mm, "end": v(409.36, 236.74) * mm, "construction": true});
            skPoint(sketch, "E154", {"position": v(425.54, 192.76) * mm});
            skCircle(sketch, "E155.MirrorC", {"center": v(415.01, 215.65) * mm, "radius": 3 * mm});
            skCircle(sketch, "E156.MirrorC", {"center": v(403.71, 257.83) * mm, "radius": 3 * mm});
            skCircle(sketch, "E157.MirrorC", {"center": v(430.45, 242.4) * mm, "radius": 3 * mm});
            skSolve(sketch);
        }
        {
            var Q0;
            Q0=qSketchRegion(id+"F37",true);
            extrude(context, id + "F38", {"entities" : qUnion([Q0]), "depth" : 3 * mm});
        }
    });
